# Revit family: Sink-Undermount-American_Standard-Aspirations-1607000.020
name_source: partatom
category: Plumbing Fixtures
units: mm (PartAtom-declared; Revit-internal decimal feet)

## family parameters
Always vertical = No
Cut with Voids When Loaded = Yes
OmniClass Number = 23.45.05.14.14
OmniClass Title = Sinks/Lavatories
Part Type = Normal
Room Calculation Point = No
Round Connector Dimension = Use Diameter
Shared = Yes
Work Plane-Based = Yes

## types (1)
- 1607000.020
    ADA Compliant = Yes
    ASME A112.18.1/CSA B125.1 = Yes
    ASME A112.19.2/CSA B45.1 = Yes
    Assembly Code = D2010410
    Basin Shape = Rectangular
    CW Connection = Yes
    CWFU = 1.5
    Cold Water Connection Diameter = 1/2"
    Cold Water Connection Radius = 1/4"
    Cold Water Connection Width = 4"
    Default Elevation = 27"
    Description = Aspirations™ Under Counter Sink
    Elevation Height = 0"
    Finish = Vitreous China-American Standard-Unfinished
    HW Connection = Yes
    HWFU = 1.5
    Height = 6 1/2"
    Hot Water Connection Diameter = 1"
    Hot Water Connection Radius = 1/4"
    Hot Water Connection Width = 4"
    Installation Type = Undermount
    Length = 20"
    Manufacturer = American Standard
    Material = Vitreous China-American Standard-020-White
    Model = 1607000.020
    Price = Prices may vary. Please consult Manufacturer Representative for most up-to-date price list.
    URL = https://www.americanstandard-us.com
    Vent Connection = No
    WFU = 2
    Warranty Information = Limited Lifetime Warranty
    Waste Connection = Yes
    Waste Connection Diameter = 1 1/2"
    Waste Connection Radius = 3/4"
    Width = 15 1/2"

## geometry (parser evidence)
native form markers: Sweep x2
no freeform markers — native parametric forms only
